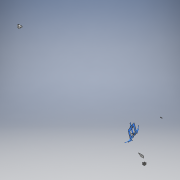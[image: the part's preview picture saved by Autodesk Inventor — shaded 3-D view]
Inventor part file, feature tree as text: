
AUTODESK INVENTOR PART (.ipt)
format: ipt  version: 2018 (Build 220112000, 112)  size: 1,342,464 bytes
history: native  units: mm
features: other x13, extrude x1, sketch x1
ambient origin geometry x8: Origin, YZ Plane, XZ Plane, XY Plane, X Axis, Y Axis, Z Axis, Center Point
bodies: Body1 (feature_tree)
feature tree (15):
  other  "for_bool.iam"
  other  "frame.ipt:1"
  other  "bracket1(body).ipt:1"
  other  "bracket2(body).ipt:1"
  other  "body-braket.ipt:1"
  other  "wire lead.ipt:1"
  other  "wire lead_MIR.ipt:1"
  other  "3-Clamp.iam:1::3-clamp body.ipt:1"
  other  "3-Clamp.iam:1::3-clamp shaft.ipt:1"
  other  "3-Clamp.iam:1::3-clamp shaft.ipt:2"
  other  "3-Clamp.iam:1::3-clamp shaft.ipt:3"
  other  "ソリッド1"
  extrude  "押し出し2"  Depth=10.0mm
  other  "面を削除4"
  sketch  "スケッチ2"
